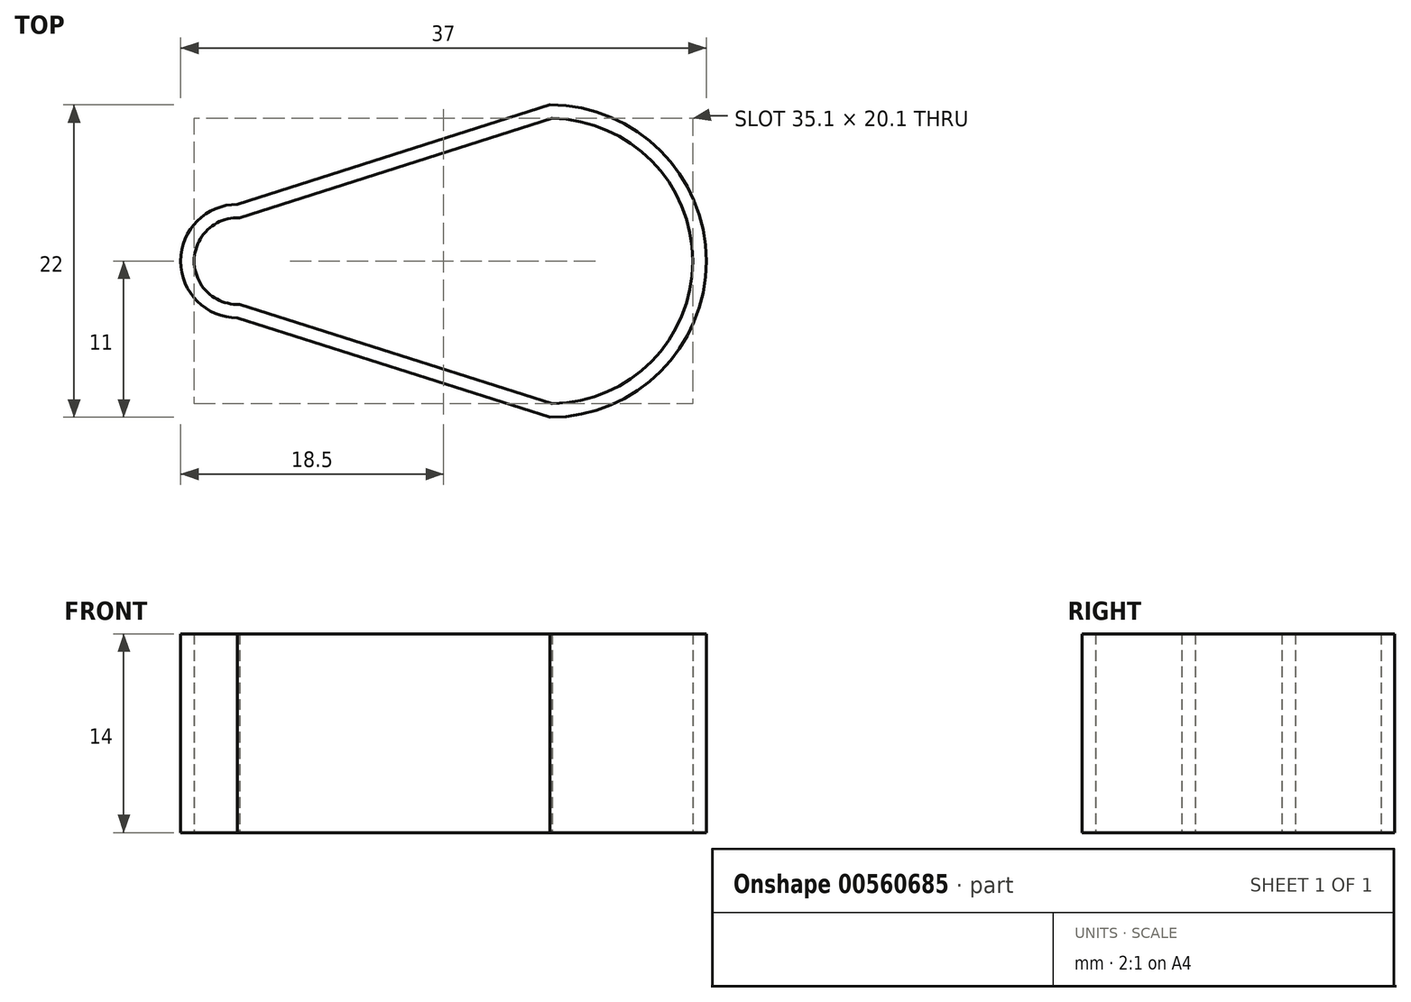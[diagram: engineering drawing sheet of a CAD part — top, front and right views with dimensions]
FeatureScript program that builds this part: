
annotation { "Feature Type Name" : "Feature", "Feature Type Description" : "" }
export const myFeature = defineFeature(function(context is Context, id is Id, definition is map)
    precondition{}
    {
        {
            var Q0;
            Q0=qCreatedBy(makeId("Top.planeOp"),FACE);
            var sketch = newSketch(context, id + "F0", { "sketchPlane" : qUnion([Q0])});
            skArc(sketch, "E0", {"start": v(-22, 4) * mm, "mid": v(-26, 0) * mm, "end": v(-22, -4) * mm});
            skArc(sketch, "E1", {"start": v(0, -11) * mm, "mid": v(11, 0) * mm, "end": v(0, 11) * mm});
            skLineSegment(sketch, "E2", {"start": v(-22, 4) * mm, "end": v(0, 11) * mm});
            skLineSegment(sketch, "E3", {"start": v(-22, -4) * mm, "end": v(0, -11) * mm});
            skSolve(sketch);
        }
        {
            var Q0;
            Q0=makeQuery(id+"F0.imprint","IMPRINT",FACE,{"disambiguationData":[TD([[makeQuery(id+"F0.imprint","IMPRINT",EDGE,{"derivedFrom":sQuery(id+"F0.wireOp",EDGE,"E0")}),1.0]])]});
            var sketch = newSketch(context, id + "F1", { "sketchPlane" : qUnion([Q0])});
            skLineSegment(sketch, "E4.0", {"start": v(-21.86, -3.05) * mm, "end": v(0.14, -10.05) * mm});
            skArc(sketch, "E4.1", {"start": v(-21.86, 3.05) * mm, "mid": v(-25.05, 0) * mm, "end": v(-21.86, -3.05) * mm});
            skLineSegment(sketch, "E4.2", {"start": v(0.14, 10.05) * mm, "end": v(-21.86, 3.05) * mm});
            skArc(sketch, "E4.3", {"start": v(0.14, -10.05) * mm, "mid": v(10.05, 0) * mm, "end": v(0.14, 10.05) * mm});
            skSolve(sketch);
        }
        {
            var Q0;
            Q0 = qSketchRegion(id + "F0", true);
            extrude(context, id + "F2", {"entities" : qUnion([Q0]), "depth" : 14 * mm, "offsetDistance" : 25 * mm});
        }
        {
            var Q0;
            Q0 = qSketchRegion(id + "F1", true);
            extrude(context, id + "F3", {"entities" : qUnion([Q0]), "operationType" : NewBodyOperationType.REMOVE, "endBound" : BoundingType.THROUGH_ALL, "depth" : 14 * mm, "offsetDistance" : 25 * mm});
        }
    });
